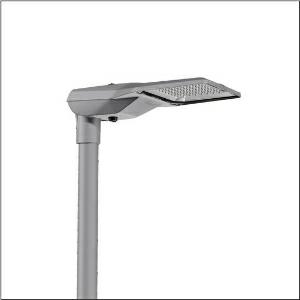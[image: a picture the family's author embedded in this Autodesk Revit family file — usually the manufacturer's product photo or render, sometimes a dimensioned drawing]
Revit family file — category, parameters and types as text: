
# Revit family: streetlight_sl_21_midi___st1_0a_5xe3d43t08nb_3e42
name_source: partatom
category: Lighting Fixtures
units: mm (PartAtom-declared; Revit-internal decimal feet)

## family parameters
Cut with Voids When Loaded = No
Host = Face
Light Source = No
Part Type = Normal
Room Calculation Point = No
Round Connector Dimension = Use Diameter
Shared = No

## types (1)
- --- (1 x LED, 23710 lm, 151.2 W, 4000K)
    Apparent Load = 151 VA
    CIE Flux Codes = 40 73 97 100 100
    Color Rendering = 70
    Color Temperature = 4000K
    Default Elevation = 1800 mm
    Description = Streetlight SL 21 midi, mast luminaire, primary light control with lens, of PMMA, primary optical cover: cover, of toughened safety glass, transparent, light distribution: ST1.0a, light emission: direct distribution, primary light characteristic: asymmetric, installation type: side-entry, post-top, LED, High Power LED, rated luminous flux: 23.710lm, luminous efficacy: 157lm/W, light colour: 740, colour temperature: 4000K, control gear: D4i, control: overheat protection, constant luminous flux control, time-dependent luminous flux control, flexible luminous flux parameterisation, pre-setting: logarithmic dimming characteristic, mains connection: 230..240V, AC, 50/60Hz, start of lifetime: 151W, end of service life: 157W, reduction: 70W, luminaire housing, of diecast aluminium, powder-coated, SITECO metallic grey (DB 702S), corrosivity category C5 high according to DIN EN ISO 12944, please order mast flange separately, inclination adjustable: 0°, 5°, 10°, 15°, sealing non-destructively replaceable, multi-level sealing system, length: 644mm, width: 335mm, height: 110mm, mast flange for spigot size: 42mm (side-entry): 5XC10008XM4, 60/48mm (side-entry/post-top): 5XC10108XM2, 76/60mm (side-entry/post-top): 5XC10108XM1, mounting height: 4..8m, Smart Interface below and above, protection rating (complete): IP66, insulation class (complete): insulation class II (safety insulation), certification: CE, ENEC, ENEC+, VDE, impact resistance: IK10, permissible operating ambient temperature for outdoor applications: -40..+50°C, standard-compliant lighting for roads and squares, packaging unit: 1 piece

Light Distribution: ST1.0a
    Height = 111 mm
    Lamp = 1 x LED
    Lamp Light Flux = 23710 lm
    Lamp Power = 151.2 W
    Lamp count = 1
    Length = 644 mm
    Luminous efficacy = 157 lm/W
    Manufacturer = Siteco
    ModVariant = No
    Model = 5XE3D43T08NB
    Number of Poles = 1
    OnlyDefault = Yes
    Power Factor = 1
    Product Name = Streetlight SL 21 midi | ST1.0a
    Product group = mast luminaire | pylon top
    ProductGroupID = 6100
    Protection Class = Protection class II
    Protection Degree = IP 66
    RLX_Detail_Level = 1
    RLX_Emergency_Light_Flux = 0 lm
    RLX_Emergency_Type = 0
    RLX_Emergency_Type_DB = No
    RlxData = <blob elided: 27121 chars, md5=d17317fa>
    Socket = socket
    Standby Power = 0 W
    System Light Flux = 23710 lm
    System Power = 151 W
    Type Comments = factory setting: luminous flux: 100 % | dim-lin: 254 | 802 mA
    Type Image = l_1004304.jpg
    URL = http://relux.com
    VarID = @adj_169939
    Voltage = 0 V
    Weight = 0.00 kg
    Width = 336 mm

## geometry (parser evidence)
native form markers: Blend x4, Sweep x9
no freeform markers — native parametric forms only
